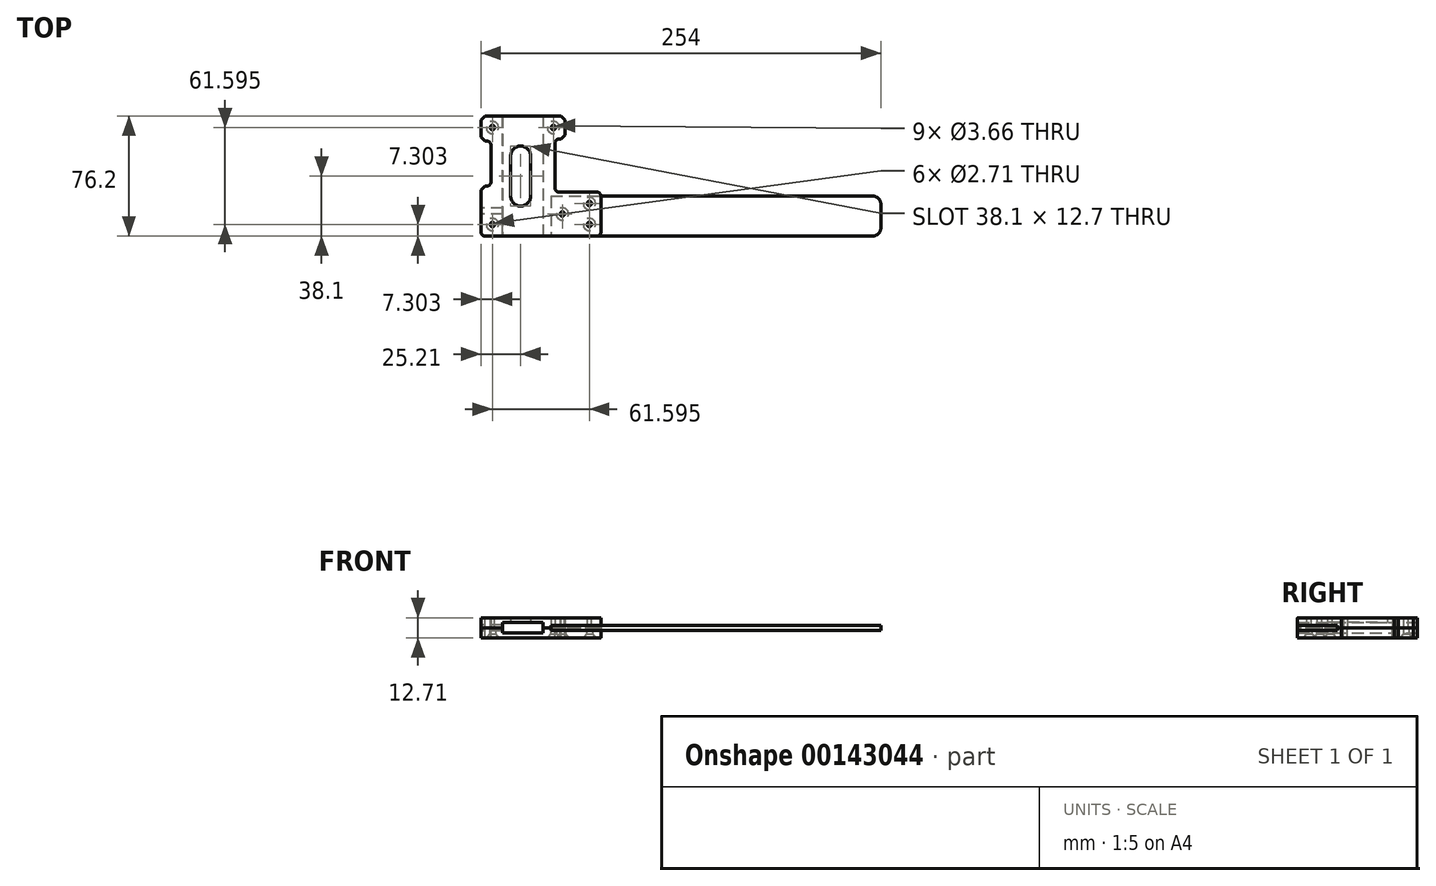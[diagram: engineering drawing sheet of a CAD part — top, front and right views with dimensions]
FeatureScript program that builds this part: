
annotation { "Feature Type Name" : "Feature", "Feature Type Description" : "" }
export const myFeature = defineFeature(function(context is Context, id is Id, definition is map)
    precondition{}
    {
        {
            var Q0;
            Q0=qCreatedBy(makeId("Top.planeOp"),FACE);
            var sketch = newSketch(context, id + "F0", { "sketchPlane" : qUnion([Q0])});
            skLineSegment(sketch, "E0.bottom", {"start": v(-38.1, 38.1) * mm, "end": v(38.1, 38.1) * mm, "construction": true});
            skLineSegment(sketch, "E0.top", {"start": v(-38.1, -38.1) * mm, "end": v(38.1, -38.1) * mm, "construction": true});
            skLineSegment(sketch, "E0.left", {"start": v(-38.1, 38.1) * mm, "end": v(-38.1, -38.1) * mm, "construction": true});
            skLineSegment(sketch, "E0.right", {"start": v(38.1, 38.1) * mm, "end": v(38.1, -38.1) * mm, "construction": true});
            skPoint(sketch, "E0.middle", {"position": v(0, 0) * mm});
            skLineSegment(sketch, "E1", {"start": v(-38.1, -38.1) * mm, "end": v(38.1, -38.1) * mm});
            skLineSegment(sketch, "E2", {"start": v(38.1, -38.1) * mm, "end": v(38.1, -10.16) * mm});
            skLineSegment(sketch, "E3", {"start": v(38.1, -10.16) * mm, "end": v(8.9, -10.16) * mm});
            skLineSegment(sketch, "E4", {"start": v(8.9, -10.16) * mm, "end": v(8.9, 23.5) * mm});
            skLineSegment(sketch, "E5", {"start": v(8.9, 23.5) * mm, "end": v(15.24, 23.5) * mm});
            skLineSegment(sketch, "E6", {"start": v(15.24, 23.5) * mm, "end": v(15.24, 38.1) * mm});
            skLineSegment(sketch, "E7", {"start": v(15.24, 38.1) * mm, "end": v(-38.1, 38.1) * mm});
            skLineSegment(sketch, "E8", {"start": v(-38.1, 38.1) * mm, "end": v(-38.1, 22.23) * mm});
            skLineSegment(sketch, "E9", {"start": v(-38.1, 22.23) * mm, "end": v(-31.75, 22.23) * mm});
            skLineSegment(sketch, "E10", {"start": v(-31.75, 22.23) * mm, "end": v(-31.75, -6.35) * mm});
            skLineSegment(sketch, "E11", {"start": v(-31.75, -6.35) * mm, "end": v(-38.1, -6.35) * mm});
            skLineSegment(sketch, "E12", {"start": v(-38.1, -6.35) * mm, "end": v(-38.1, -38.1) * mm});
            skSolve(sketch);
        }
        {
            var Q0;
            Q0 = qSketchRegion(id + "F0", true);
            extrude(context, id + "F1", {"entities" : qUnion([Q0]), "endBound" : BoundingType.SYMMETRIC, "depth" : 6.35 * mm});
        }
        {
            var Q0;
            Q0=makeQuery(id+"F1.opExtrude","SWEPT_EDGE",EDGE,{"disambiguationData":[OSD([sQuery(id+"F0.wireOp",EDGE,"E7"),sQuery(id+"F0.wireOp",EDGE,"E8")])]});
            var Q1;
            Q1=makeQuery(id+"F1.opExtrude","SWEPT_EDGE",EDGE,{"disambiguationData":[OSD([sQuery(id+"F0.wireOp",EDGE,"E8"),sQuery(id+"F0.wireOp",EDGE,"E9")])]});
            var Q2;
            Q2=makeQuery(id+"F1.opExtrude","SWEPT_EDGE",EDGE,{"disambiguationData":[OSD([sQuery(id+"F0.wireOp",EDGE,"E11"),sQuery(id+"F0.wireOp",EDGE,"E12")])]});
            var Q3;
            Q3=makeQuery(id+"F1.opExtrude","SWEPT_EDGE",EDGE,{"disambiguationData":[OSD([sQuery(id+"F0.wireOp",EDGE,"E5"),sQuery(id+"F0.wireOp",EDGE,"E6")])]});
            var Q4;
            Q4=makeQuery(id+"F1.opExtrude","SWEPT_EDGE",EDGE,{"disambiguationData":[OSD([sQuery(id+"F0.wireOp",EDGE,"E6"),sQuery(id+"F0.wireOp",EDGE,"E7")])]});
            chamfer(context, id + "F2", {"entities" : qUnion([Q0, Q1, Q2, Q3, Q4]), "width" : 2.54 * mm, "tangentPropagation" : true});
        }
        {
            var Q0;
            Q0=makeQuery(id+"F1.opExtrude","SWEPT_EDGE",EDGE,{"disambiguationData":[OSD([sQuery(id+"F0.wireOp",EDGE,"E9"),sQuery(id+"F0.wireOp",EDGE,"E10")])]});
            var Q1;
            Q1=makeQuery(id+"F1.opExtrude","SWEPT_EDGE",EDGE,{"disambiguationData":[OSD([sQuery(id+"F0.wireOp",EDGE,"E10"),sQuery(id+"F0.wireOp",EDGE,"E11")])]});
            var Q2;
            Q2=makeQuery(id+"F1.opExtrude","SWEPT_EDGE",EDGE,{"disambiguationData":[OSD([sQuery(id+"F0.wireOp",EDGE,"E4"),sQuery(id+"F0.wireOp",EDGE,"E5")])]});
            var Q3;
            Q3=makeQuery(id+"F1.opExtrude","SWEPT_EDGE",EDGE,{"disambiguationData":[OSD([sQuery(id+"F0.wireOp",EDGE,"E3"),sQuery(id+"F0.wireOp",EDGE,"E4")])]});
            var Q4;
            Q4=makeQuery(id+"F1.opExtrude","SWEPT_EDGE",EDGE,{"disambiguationData":[OSD([sQuery(id+"F0.wireOp",EDGE,"E2"),sQuery(id+"F0.wireOp",EDGE,"E3")])]});
            var Q5;
            Q5=makeQuery(id+"F1.opExtrude","SWEPT_EDGE",EDGE,{"disambiguationData":[OSD([sQuery(id+"F0.wireOp",EDGE,"E1"),sQuery(id+"F0.wireOp",EDGE,"E2")])]});
            var Q6;
            Q6=makeQuery(id+"F1.opExtrude","SWEPT_EDGE",EDGE,{"disambiguationData":[OSD([sQuery(id+"F0.wireOp",EDGE,"E1"),sQuery(id+"F0.wireOp",EDGE,"E12")])]});
            fillet(context, id + "F3", {"entities" : qUnion([Q0, Q1, Q2, Q3, Q4, Q5, Q6]), "radius" : 2.54 * mm, "tangentPropagation" : true, "allowEdgeOverflow" : false});
        }
        {
            var Q0;
            Q0=makeQuery(id+"F1.opExtrude","CAP_FACE",FACE,{"disambiguationData":[OSD([sQuery(id+"F0.wireOp",EDGE,"E1"),sQuery(id+"F0.wireOp",EDGE,"E2"),sQuery(id+"F0.wireOp",EDGE,"E3"),sQuery(id+"F0.wireOp",EDGE,"E4"),sQuery(id+"F0.wireOp",EDGE,"E5"),sQuery(id+"F0.wireOp",EDGE,"E6"),sQuery(id+"F0.wireOp",EDGE,"E7"),sQuery(id+"F0.wireOp",EDGE,"E8"),sQuery(id+"F0.wireOp",EDGE,"E9"),sQuery(id+"F0.wireOp",EDGE,"E10"),sQuery(id+"F0.wireOp",EDGE,"E11"),sQuery(id+"F0.wireOp",EDGE,"E12")])],"isStart":true});
            extrude(context, id + "F4", {"entities" : qUnion([Q0]), "depth" : 6.35 * mm});
        }
        {
            var Q0;
            Q0=makeQuery(id+"F1.opExtrude","CAP_FACE",FACE,{"disambiguationData":[OSD([sQuery(id+"F0.wireOp",EDGE,"E1"),sQuery(id+"F0.wireOp",EDGE,"E2"),sQuery(id+"F0.wireOp",EDGE,"E3"),sQuery(id+"F0.wireOp",EDGE,"E4"),sQuery(id+"F0.wireOp",EDGE,"E5"),sQuery(id+"F0.wireOp",EDGE,"E6"),sQuery(id+"F0.wireOp",EDGE,"E7"),sQuery(id+"F0.wireOp",EDGE,"E8"),sQuery(id+"F0.wireOp",EDGE,"E9"),sQuery(id+"F0.wireOp",EDGE,"E10"),sQuery(id+"F0.wireOp",EDGE,"E11"),sQuery(id+"F0.wireOp",EDGE,"E12")])],"isStart":true});
            var sketch = newSketch(context, id + "F5", { "sketchPlane" : qUnion([Q0])});
            skLineSegment(sketch, "E13.bottom", {"start": v(1.46, 38.1) * mm, "end": v(-24.32, 38.1) * mm});
            skLineSegment(sketch, "E13.top", {"start": v(1.46, -38.1) * mm, "end": v(-24.32, -38.1) * mm});
            skLineSegment(sketch, "E13.left", {"start": v(1.46, 38.1) * mm, "end": v(1.46, -38.1) * mm});
            skLineSegment(sketch, "E13.right", {"start": v(-24.32, 38.1) * mm, "end": v(-24.32, -38.1) * mm});
            skLineSegment(sketch, "E14", {"start": v(8.9, -6.67) * mm, "end": v(-31.75, -6.67) * mm, "construction": true});
            skLineSegment(sketch, "E15", {"start": v(-11.43, -6.67) * mm, "end": v(-11.43, -38.1) * mm, "construction": true});
            skSolve(sketch);
        }
        {
            var Q0;
            Q0 = qSketchRegion(id + "F5", true);
            extrude(context, id + "F6", {"entities" : qUnion([Q0]), "operationType" : NewBodyOperationType.REMOVE, "oppositeDirection" : true, "depth" : 3.3 * mm, "hasSecondDirection" : true, "secondDirectionOppositeDirection" : false, "secondDirectionDepth" : 3.3 * mm});
        }
        {
            var Q0;
            {var subQ0=sQuery(id+"F0.wireOp",EDGE,"E6");var subQ1=sQuery(id+"F0.wireOp",EDGE,"E5");var subQ2=sQuery(id+"F0.wireOp",EDGE,"E2");var subQ3=sQuery(id+"F0.wireOp",EDGE,"E1");var subQ4=sQuery(id+"F0.wireOp",EDGE,"E7");var subQ5=sQuery(id+"F0.wireOp",EDGE,"E3");var subQ6=sQuery(id+"F0.wireOp",EDGE,"E4");Q0=makeQuery(id+"F6.boolean.opBoolean","SPLIT",FACE,{"disambiguationData":[TD([makeQuery(id+"F1.opExtrude","SWEPT_FACE",FACE,{"disambiguationData":[OSD([subQ2])]})])],"derivedFrom":makeQuery(id+"F1.opExtrude","CAP_FACE",FACE,{"disambiguationData":[OSD([subQ3,subQ2,subQ5,subQ6,subQ1,subQ0,subQ4,sQuery(id+"F0.wireOp",EDGE,"E8"),sQuery(id+"F0.wireOp",EDGE,"E9"),sQuery(id+"F0.wireOp",EDGE,"E10"),sQuery(id+"F0.wireOp",EDGE,"E11"),sQuery(id+"F0.wireOp",EDGE,"E12")])],"isStart":true})});}
            var sketch = newSketch(context, id + "F7", { "sketchPlane" : qUnion([Q0])});
            skLineSegment(sketch, "E16.bottom", {"start": v(38.1, 38.1) * mm, "end": v(6.35, 38.1) * mm});
            skLineSegment(sketch, "E16.top", {"start": v(38.1, 12.7) * mm, "end": v(6.35, 12.7) * mm});
            skLineSegment(sketch, "E16.left", {"start": v(38.1, 38.1) * mm, "end": v(38.1, 12.7) * mm});
            skLineSegment(sketch, "E16.right", {"start": v(6.35, 38.1) * mm, "end": v(6.35, 12.7) * mm});
            skSolve(sketch);
        }
        {
            var Q0;
            Q0 = qSketchRegion(id + "F7", true);
            extrude(context, id + "F8", {"entities" : qUnion([Q0]), "operationType" : NewBodyOperationType.REMOVE, "oppositeDirection" : true, "depth" : 1.65 * mm, "hasSecondDirection" : true, "secondDirectionOppositeDirection" : false, "secondDirectionDepth" : 1.65 * mm});
        }
        {
            var Q0;
            Q0=makeQuery(id+"F1.opExtrude","CAP_FACE",FACE,{"disambiguationData":[OSD([sQuery(id+"F0.wireOp",EDGE,"E1"),sQuery(id+"F0.wireOp",EDGE,"E2"),sQuery(id+"F0.wireOp",EDGE,"E3"),sQuery(id+"F0.wireOp",EDGE,"E4"),sQuery(id+"F0.wireOp",EDGE,"E5"),sQuery(id+"F0.wireOp",EDGE,"E6"),sQuery(id+"F0.wireOp",EDGE,"E7"),sQuery(id+"F0.wireOp",EDGE,"E8"),sQuery(id+"F0.wireOp",EDGE,"E9"),sQuery(id+"F0.wireOp",EDGE,"E10"),sQuery(id+"F0.wireOp",EDGE,"E11"),sQuery(id+"F0.wireOp",EDGE,"E12")])],"isStart":false});
            var sketch = newSketch(context, id + "F9", { "sketchPlane" : qUnion([Q0])});
            skLineSegment(sketch, "E17.bottom", {"start": v(-30.8, 30.8) * mm, "end": v(7.94, 30.8) * mm, "construction": true});
            skLineSegment(sketch, "E17.top", {"start": v(-30.8, -30.8) * mm, "end": v(7.94, -30.8) * mm, "construction": true});
            skLineSegment(sketch, "E17.left", {"start": v(-30.8, 30.8) * mm, "end": v(-30.8, -30.8) * mm, "construction": true});
            skLineSegment(sketch, "E17.right", {"start": v(7.94, 30.8) * mm, "end": v(7.94, -30.8) * mm, "construction": true});
            skLineSegment(sketch, "E18", {"start": v(-30.8, 30.8) * mm, "end": v(-38.1, 30.8) * mm, "construction": true});
            skLineSegment(sketch, "E19", {"start": v(7.94, 30.8) * mm, "end": v(15.24, 30.8) * mm, "construction": true});
            skLineSegment(sketch, "E20", {"start": v(-30.8, -30.8) * mm, "end": v(-38.1, -30.8) * mm, "construction": true});
            skLineSegment(sketch, "E21", {"start": v(-30.8, 30.8) * mm, "end": v(-30.8, 38.1) * mm, "construction": true});
            skLineSegment(sketch, "E22", {"start": v(-30.8, -30.8) * mm, "end": v(-30.8, -38.1) * mm, "construction": true});
            skLineSegment(sketch, "E23", {"start": v(7.94, -30.8) * mm, "end": v(30.8, -30.8) * mm, "construction": true});
            skLineSegment(sketch, "E24", {"start": v(7.94, -17.46) * mm, "end": v(30.8, -17.46) * mm, "construction": true});
            skLineSegment(sketch, "E25", {"start": v(30.8, -17.46) * mm, "end": v(30.8, -30.8) * mm, "construction": true});
            skLineSegment(sketch, "E26", {"start": v(30.8, -30.8) * mm, "end": v(30.8, -38.1) * mm, "construction": true});
            skLineSegment(sketch, "E27", {"start": v(30.8, -17.46) * mm, "end": v(30.8, -10.16) * mm, "construction": true});
            skLineSegment(sketch, "E28", {"start": v(30.8, -17.46) * mm, "end": v(38.1, -17.46) * mm, "construction": true});
            skLineSegment(sketch, "E29", {"start": v(30.8, -30.8) * mm, "end": v(38.1, -30.8) * mm, "construction": true});
            skLineSegment(sketch, "E30", {"start": v(13.65, -30.8) * mm, "end": v(13.65, -17.46) * mm, "construction": true});
            skLineSegment(sketch, "E31", {"start": v(13.65, -24.13) * mm, "end": v(6.35, -24.13) * mm, "construction": true});
            skSolve(sketch);
        }
        {
            var Q0;
            Q0=sQuery(id+"F9.wireOp",VERTEX,"E18.start");
            var Q1;
            Q1=sQuery(id+"F9.wireOp",VERTEX,"E19.start");
            var Q2;
            Q2=sQuery(id+"F9.wireOp",VERTEX,"E22.start");
            var Q3;
            Q3=sQuery(id+"F9.wireOp",VERTEX,"E31.start");
            var Q4;
            Q4=sQuery(id+"F9.wireOp",VERTEX,"E24.end");
            var Q5;
            Q5=sQuery(id+"F9.wireOp",VERTEX,"E23.end");
            var Q6;
            Q6=makeQuery(id+"F1.opExtrude","SWEPT_BODY",BODY,{"disambiguationData":[OSD([sQuery(id+"F0.wireOp",EDGE,"E1"),sQuery(id+"F0.wireOp",EDGE,"E2"),sQuery(id+"F0.wireOp",EDGE,"E3"),sQuery(id+"F0.wireOp",EDGE,"E4"),sQuery(id+"F0.wireOp",EDGE,"E5"),sQuery(id+"F0.wireOp",EDGE,"E6"),sQuery(id+"F0.wireOp",EDGE,"E7"),sQuery(id+"F0.wireOp",EDGE,"E8"),sQuery(id+"F0.wireOp",EDGE,"E9"),sQuery(id+"F0.wireOp",EDGE,"E10"),sQuery(id+"F0.wireOp",EDGE,"E11"),sQuery(id+"F0.wireOp",EDGE,"E12")])]});
            hole(context, id + "F10", {"style" : HoleStyle.SIMPLE, "endStyle" : HoleEndStyle.THROUGH, "standardTappedOrClearance" : lookupTablePath({ "standard" : "ANSI", "engagement" : "75%", "pitch" : "32 tpi", "size" : "#6", "type" : "Tapped" }), "standardBlindInLast" : lookupTablePath({ "standard" : "ANSI", "engagement" : "75%", "pitch" : "32 tpi", "size" : "#6", "type" : "Tapped" }), "holeDiameter" : 2.7 * mm, "locations" : qUnion([Q0, Q1, Q2, Q3, Q4, Q5]), "scope" : qUnion([Q6]), "isTappedThrough" : true, "majorDiameter" : 3.5 * mm, "showTappedDepth" : true});
        }
        {
            var Q0;
            Q0=makeQuery(id+"F4.opExtrude","CAP_FACE",FACE,{"disambiguationData":[OSD([sQuery(id+"F0.wireOp",EDGE,"E1"),sQuery(id+"F0.wireOp",EDGE,"E2"),sQuery(id+"F0.wireOp",EDGE,"E3"),sQuery(id+"F0.wireOp",EDGE,"E4"),sQuery(id+"F0.wireOp",EDGE,"E5"),sQuery(id+"F0.wireOp",EDGE,"E6"),sQuery(id+"F0.wireOp",EDGE,"E7"),sQuery(id+"F0.wireOp",EDGE,"E8"),sQuery(id+"F0.wireOp",EDGE,"E9"),sQuery(id+"F0.wireOp",EDGE,"E10"),sQuery(id+"F0.wireOp",EDGE,"E11"),sQuery(id+"F0.wireOp",EDGE,"E12")])],"isStart":false});
            var sketch = newSketch(context, id + "F11", { "sketchPlane" : qUnion([Q0])});
            skPoint(sketch, "E32", {"position": v(-30.8, 30.8) * mm});
            skPoint(sketch, "E33", {"position": v(-30.8, -30.8) * mm});
            skPoint(sketch, "E34", {"position": v(7.94, -30.8) * mm});
            skPoint(sketch, "E35", {"position": v(13.65, 24.13) * mm});
            skPoint(sketch, "E36", {"position": v(30.8, 30.8) * mm});
            skPoint(sketch, "E37", {"position": v(30.8, 17.46) * mm});
            skSolve(sketch);
        }
        {
            var Q0;
            Q0=sQuery(id+"F11.wireOp",VERTEX,"E33");
            var Q1;
            Q1=sQuery(id+"F11.wireOp",VERTEX,"E32");
            var Q2;
            Q2=sQuery(id+"F11.wireOp",VERTEX,"E34");
            var Q3;
            Q3=sQuery(id+"F11.wireOp",VERTEX,"E35");
            var Q4;
            Q4=sQuery(id+"F11.wireOp",VERTEX,"E37");
            var Q5;
            Q5=sQuery(id+"F11.wireOp",VERTEX,"E36");
            var Q6;
            Q6=makeQuery(id+"F4.opExtrude","SWEPT_BODY",BODY,{"disambiguationData":[OSD([sQuery(id+"F0.wireOp",EDGE,"E1"),sQuery(id+"F0.wireOp",EDGE,"E2"),sQuery(id+"F0.wireOp",EDGE,"E3"),sQuery(id+"F0.wireOp",EDGE,"E4"),sQuery(id+"F0.wireOp",EDGE,"E5"),sQuery(id+"F0.wireOp",EDGE,"E6"),sQuery(id+"F0.wireOp",EDGE,"E7"),sQuery(id+"F0.wireOp",EDGE,"E8"),sQuery(id+"F0.wireOp",EDGE,"E9"),sQuery(id+"F0.wireOp",EDGE,"E10"),sQuery(id+"F0.wireOp",EDGE,"E11"),sQuery(id+"F0.wireOp",EDGE,"E12")])]});
            hole(context, id + "F12", {"style" : HoleStyle.C_SINK, "endStyle" : HoleEndStyle.THROUGH, "standardTappedOrClearance" : lookupTablePath({ "standard" : "ANSI", "fit" : "Close", "size" : "#6", "type" : "Clearance" }), "standardBlindInLast" : lookupTablePath({ "fit" : "Close", "standard" : "ANSI", "size" : "#6", "type" : "Clearance" }), "holeDiameter" : 3.66 * mm, "cSinkDiameter" : 7.8 * mm, "cSinkAngle" : 82 * degree, "locations" : qUnion([Q0, Q1, Q2, Q3, Q4, Q5]), "scope" : qUnion([Q6]), "isTappedThrough" : true});
        }
        {
            var Q0;
            Q0=makeQuery(id+"F6.boolean.opBoolean","COPY",FACE,{"derivedFrom":makeQuery(id+"F6.opExtrude","CAP_FACE",FACE,{"disambiguationData":[OSD([sQuery(id+"F5.wireOp",EDGE,"E13.bottom"),sQuery(id+"F5.wireOp",EDGE,"E13.top"),sQuery(id+"F5.wireOp",EDGE,"E13.left"),sQuery(id+"F5.wireOp",EDGE,"E13.right")])],"isStart":false})});
            var sketch = newSketch(context, id + "F13", { "sketchPlane" : qUnion([Q0])});
            skArc(sketch, "E38", {"start": v(-6.54, 12.7) * mm, "mid": v(-12.9, 19.05) * mm, "end": v(-19.24, 12.7) * mm});
            skArc(sketch, "E39", {"start": v(-6.54, -12.7) * mm, "mid": v(-12.9, -19.05) * mm, "end": v(-19.24, -12.7) * mm});
            skLineSegment(sketch, "E40", {"start": v(-19.24, -12.7) * mm, "end": v(-19.24, 12.7) * mm});
            skLineSegment(sketch, "E41", {"start": v(-6.54, 12.7) * mm, "end": v(-6.54, -12.7) * mm});
            skLineSegment(sketch, "E42", {"start": v(-12.9, 12.7) * mm, "end": v(-12.9, 38.1) * mm, "construction": true});
            skLineSegment(sketch, "E43", {"start": v(-12.9, -12.7) * mm, "end": v(-12.9, -38.1) * mm, "construction": true});
            skSolve(sketch);
        }
        {
            var Q0;
            Q0 = qSketchRegion(id + "F13", true);
            extrude(context, id + "F14", {"entities" : qUnion([Q0]), "operationType" : NewBodyOperationType.REMOVE, "oppositeDirection" : true, "depth" : 25.4 * mm});
        }
        {
            var Q0;
            Q0=makeQuery(id+"F8.boolean.opBoolean","COPY",FACE,{"derivedFrom":makeQuery(id+"F8.opExtrude","CAP_FACE",FACE,{"disambiguationData":[OSD([sQuery(id+"F7.wireOp",EDGE,"E16.bottom"),sQuery(id+"F7.wireOp",EDGE,"E16.top"),sQuery(id+"F7.wireOp",EDGE,"E16.left"),sQuery(id+"F7.wireOp",EDGE,"E16.right")])],"isStart":true})});
            var sketch = newSketch(context, id + "F15", { "sketchPlane" : qUnion([Q0])});
            skLineSegment(sketch, "E44.bottom", {"start": v(6.35, -38.1) * mm, "end": v(215.9, -38.1) * mm});
            skLineSegment(sketch, "E44.top", {"start": v(6.35, -12.7) * mm, "end": v(215.9, -12.7) * mm});
            skLineSegment(sketch, "E44.left", {"start": v(6.35, -38.1) * mm, "end": v(6.35, -12.7) * mm});
            skLineSegment(sketch, "E44.right", {"start": v(215.9, -38.1) * mm, "end": v(215.9, -12.7) * mm});
            skSolve(sketch);
        }
        {
            var Q0;
            Q0 = qSketchRegion(id + "F15", true);
            extrude(context, id + "F16", {"entities" : qUnion([Q0]), "depth" : 3.17 * mm});
        }
        {
            var Q0;
            Q0=makeQuery(id+"F16.opExtrude","SWEPT_EDGE",EDGE,{"disambiguationData":[OSD([sQuery(id+"F15.wireOp",EDGE,"E44.bottom"),sQuery(id+"F15.wireOp",EDGE,"E44.right")])]});
            var Q1;
            Q1=makeQuery(id+"F16.opExtrude","SWEPT_EDGE",EDGE,{"disambiguationData":[OSD([sQuery(id+"F15.wireOp",EDGE,"E44.top"),sQuery(id+"F15.wireOp",EDGE,"E44.right")])]});
            fillet(context, id + "F17", {"entities" : qUnion([Q0, Q1]), "radius" : 5.08 * mm, "tangentPropagation" : true, "allowEdgeOverflow" : false});
        }
        {
            var Q0;
            Q0=sQuery(id+"F9.wireOp",VERTEX,"E31.start");
            var Q1;
            Q1=sQuery(id+"F9.wireOp",VERTEX,"E26.start");
            var Q2;
            Q2=sQuery(id+"F9.wireOp",VERTEX,"E28.start");
            var Q3;
            Q3=makeQuery(id+"F16.opExtrude","SWEPT_BODY",BODY,{"disambiguationData":[OSD([sQuery(id+"F15.wireOp",EDGE,"E44.bottom"),sQuery(id+"F15.wireOp",EDGE,"E44.top"),sQuery(id+"F15.wireOp",EDGE,"E44.left"),sQuery(id+"F15.wireOp",EDGE,"E44.right")])]});
            hole(context, id + "F18", {"style" : HoleStyle.SIMPLE, "endStyle" : HoleEndStyle.THROUGH, "standardTappedOrClearance" : lookupTablePath({ "standard" : "ANSI", "fit" : "Close", "size" : "#6", "type" : "Clearance" }), "standardBlindInLast" : lookupTablePath({ "fit" : "Close", "standard" : "ANSI", "size" : "#6", "type" : "Clearance" }), "holeDiameter" : 3.66 * mm, "locations" : qUnion([Q0, Q1, Q2]), "scope" : qUnion([Q3]), "isTappedThrough" : true});
        }
        {
            var Q0;
            Q0=makeQuery(id+"F1.opExtrude","SWEPT_FACE",FACE,{"disambiguationData":[OSD([sQuery(id+"F0.wireOp",EDGE,"E12")])]});
            var sketch = newSketch(context, id + "F19", { "sketchPlane" : qUnion([Q0])});
            skPoint(sketch, "E45", {"position": v(22.23, -3.18) * mm});
            skSolve(sketch);
        }
        {
            var Q0;
            Q0=sQuery(id+"F19.wireOp",VERTEX,"E45");
            var Q1;
            Q1=makeQuery(id+"F4.opExtrude","SWEPT_BODY",BODY,{"disambiguationData":[OSD([sQuery(id+"F0.wireOp",EDGE,"E1"),sQuery(id+"F0.wireOp",EDGE,"E2"),sQuery(id+"F0.wireOp",EDGE,"E3"),sQuery(id+"F0.wireOp",EDGE,"E4"),sQuery(id+"F0.wireOp",EDGE,"E5"),sQuery(id+"F0.wireOp",EDGE,"E6"),sQuery(id+"F0.wireOp",EDGE,"E7"),sQuery(id+"F0.wireOp",EDGE,"E8"),sQuery(id+"F0.wireOp",EDGE,"E9"),sQuery(id+"F0.wireOp",EDGE,"E10"),sQuery(id+"F0.wireOp",EDGE,"E11"),sQuery(id+"F0.wireOp",EDGE,"E12")])]});
            var Q2;
            Q2=makeQuery(id+"F1.opExtrude","SWEPT_BODY",BODY,{"disambiguationData":[OSD([sQuery(id+"F0.wireOp",EDGE,"E1"),sQuery(id+"F0.wireOp",EDGE,"E2"),sQuery(id+"F0.wireOp",EDGE,"E3"),sQuery(id+"F0.wireOp",EDGE,"E4"),sQuery(id+"F0.wireOp",EDGE,"E5"),sQuery(id+"F0.wireOp",EDGE,"E6"),sQuery(id+"F0.wireOp",EDGE,"E7"),sQuery(id+"F0.wireOp",EDGE,"E8"),sQuery(id+"F0.wireOp",EDGE,"E9"),sQuery(id+"F0.wireOp",EDGE,"E10"),sQuery(id+"F0.wireOp",EDGE,"E11"),sQuery(id+"F0.wireOp",EDGE,"E12")])]});
            hole(context, id + "F20", {"style" : HoleStyle.SIMPLE, "endStyle" : HoleEndStyle.BLIND, "standardTappedOrClearance" : lookupTablePath({ "standard" : "ANSI", "engagement" : "75%", "pitch" : "24 tpi", "size" : "#10", "type" : "Tapped" }), "standardBlindInLast" : lookupTablePath({ "standard" : "ANSI", "engagement" : "75%", "pitch" : "24 tpi", "size" : "#10", "type" : "Tapped" }), "holeDiameter" : 3.8 * mm, "holeDepth" : 25.4 * mm, "locations" : qUnion([Q0]), "scope" : qUnion([Q1, Q2]), "majorDiameter" : 4.83 * mm});
        }
    });
